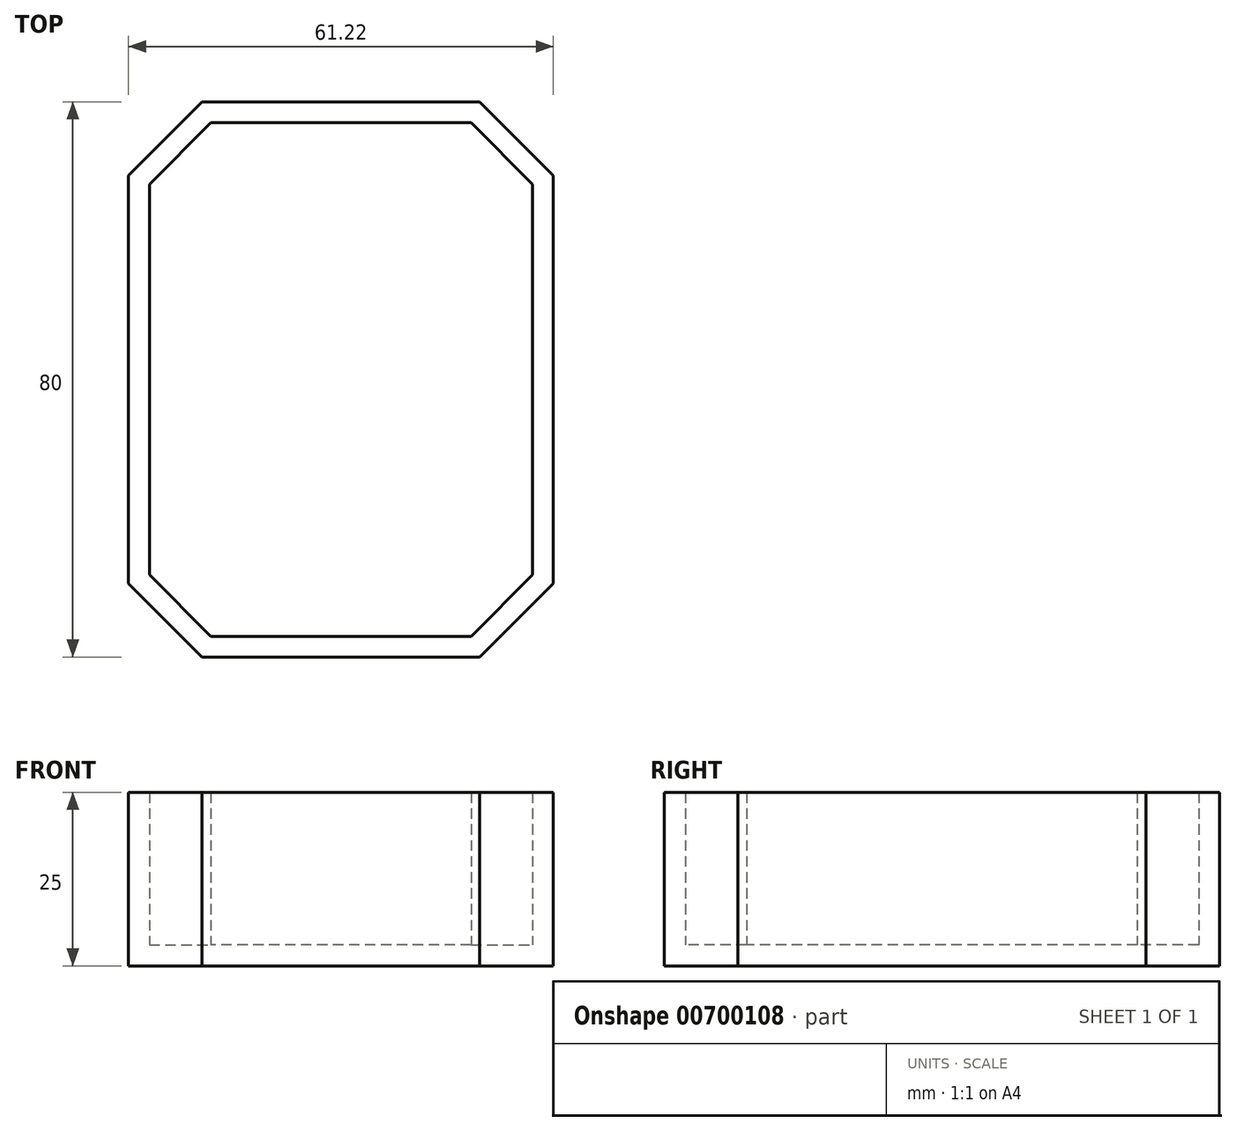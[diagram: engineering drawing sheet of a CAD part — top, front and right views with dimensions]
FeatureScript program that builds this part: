
annotation { "Feature Type Name" : "Feature", "Feature Type Description" : "" }
export const myFeature = defineFeature(function(context is Context, id is Id, definition is map)
    precondition{}
    {
        {
            var Q0;
            Q0=qCreatedBy(makeId("Top.planeOp"),FACE);
            var sketch = newSketch(context, id + "F0", { "sketchPlane" : qUnion([Q0])});
            skLineSegment(sketch, "E0", {"start": v(0, 40) * mm, "end": v(0, -40) * mm, "construction": true});
            skLineSegment(sketch, "E1", {"start": v(0, -40) * mm, "end": v(20, -40) * mm});
            skLineSegment(sketch, "E2", {"start": v(20, -40) * mm, "end": v(30.6, -29.4) * mm});
            skLineSegment(sketch, "E3", {"start": v(30.6, -29.4) * mm, "end": v(30.6, 29.4) * mm});
            skLineSegment(sketch, "E4", {"start": v(30.6, 29.4) * mm, "end": v(20, 40) * mm});
            skLineSegment(sketch, "E5", {"start": v(20, 40) * mm, "end": v(0, 40) * mm});
            skLineSegment(sketch, "E6.MirrorCS", {"start": v(-20, 40) * mm, "end": v(0, 40) * mm});
            skLineSegment(sketch, "E7.MirrorCS", {"start": v(-30.6, 29.4) * mm, "end": v(-20, 40) * mm});
            skLineSegment(sketch, "E8.MirrorCS", {"start": v(-30.6, -29.4) * mm, "end": v(-30.6, 29.4) * mm});
            skLineSegment(sketch, "E9.MirrorCS", {"start": v(-20, -40) * mm, "end": v(-30.6, -29.4) * mm});
            skLineSegment(sketch, "E10.MirrorCS", {"start": v(0, -40) * mm, "end": v(-20, -40) * mm});
            skLineSegment(sketch, "E11", {"start": v(-30.6, 0) * mm, "end": v(30.6, 0) * mm, "construction": true});
            skLineSegment(sketch, "E12.0", {"start": v(-27.6, -28.15) * mm, "end": v(-27.6, 28.15) * mm});
            skLineSegment(sketch, "E12.1", {"start": v(-18.76, -37) * mm, "end": v(-27.6, -28.15) * mm});
            skLineSegment(sketch, "E12.2", {"start": v(-27.6, 28.15) * mm, "end": v(-18.76, 37) * mm});
            skLineSegment(sketch, "E12.3", {"start": v(0, -37) * mm, "end": v(-18.76, -37) * mm});
            skLineSegment(sketch, "E12.4", {"start": v(0, -37) * mm, "end": v(18.76, -37) * mm});
            skLineSegment(sketch, "E12.5", {"start": v(18.76, -37) * mm, "end": v(27.6, -28.15) * mm});
            skLineSegment(sketch, "E12.6", {"start": v(-18.76, 37) * mm, "end": v(0, 37) * mm});
            skLineSegment(sketch, "E12.7", {"start": v(18.76, 37) * mm, "end": v(0, 37) * mm});
            skLineSegment(sketch, "E12.8", {"start": v(27.6, 28.15) * mm, "end": v(18.76, 37) * mm});
            skLineSegment(sketch, "E12.9", {"start": v(27.6, -28.15) * mm, "end": v(27.6, 28.15) * mm});
            skSolve(sketch);
        }
        {
            var Q0;
            Q0 = qSketchRegion(id + "F0", true);
            var Q1;
            Q1=makeQuery(id+"F0.imprint","IMPRINT",FACE,{"disambiguationData":[TD([[makeQuery(id+"F0.imprint","IMPRINT",EDGE,{"derivedFrom":sQuery(id+"F0.wireOp",EDGE,"E12.0")}),-1.0]])]});
            extrude(context, id + "F1", {"entities" : qUnion([Q0, Q1]), "depth" : 3 * mm, "offsetDistance" : 25 * mm});
        }
        {
            var Q0;
            Q0=makeQuery(id+"F0.imprint","IMPRINT",FACE,{"disambiguationData":[TD([[makeQuery(id+"F0.imprint","IMPRINT",EDGE,{"derivedFrom":sQuery(id+"F0.wireOp",EDGE,"E1")}),1.0]])]});
            extrude(context, id + "F2", {"entities" : qUnion([Q0]), "operationType" : NewBodyOperationType.ADD, "depth" : 25 * mm, "offsetDistance" : 25 * mm});
        }
    });
